# Revit family: Flush Plate for B-T-W Pans
name_source: partatom
category: Plumbing Fixtures
units: mm (PartAtom-declared; Revit-internal decimal feet)

## family parameters
Always vertical = Yes
Cut with Voids When Loaded = No
Enable Cutting in Views = No
Host = Wall
Maintain Annotation Orientation = No
OmniClass Number = 23.45.00.00
OmniClass Title = Sanitary, Laundry, and Cleaning Equipment
Part Type = Normal
Room Calculation Point = No
Round Connector Dimension = Use Diameter
Shared = No

## types (3) — shared parameters
Category = Flush Plate
Manufacturer = Lecico SA
Material = ABS Plastic
Model = Flush Plate for BTW pans
Technical Dimensions = W236 x H152 x D06mm
URL = https://www.lecicosa.co.za
zero-valued in all types: Default Elevation

## per-type parameters (varying)
| type | Plate Colour | Product Code |
| Black | Gloss Black | LECFLUPLABBLABC |
| White | Gloss White | LECFLUPLABWHIBC |
| Chrome | Chrome | LECFLUPLABCHRBC |

note: column(s) folded — value = type name in every type: Colour

## geometry (parser evidence)
native form markers: Sweep x5
no freeform markers — native parametric forms only
